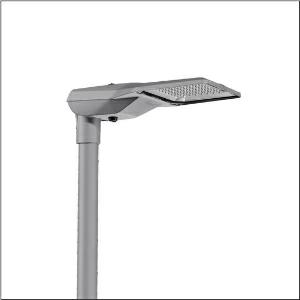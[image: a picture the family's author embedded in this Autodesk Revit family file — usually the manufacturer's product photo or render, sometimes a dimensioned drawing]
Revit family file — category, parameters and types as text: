
# Revit family: streetlight_sl_21_iq_midi___st1_0a_5xe3d31y08mb_3ca9
name_source: partatom
category: Lighting Fixtures
units: mm (PartAtom-declared; Revit-internal decimal feet)

## family parameters
Cut with Voids When Loaded = No
Host = Face
Light Source = No
Part Type = Normal
Room Calculation Point = No
Round Connector Dimension = Use Diameter
Shared = No

## types (1)
- --- (1 x LED, 18340 lm, 129.3 W, 3000K)
    Apparent Load = 129 VA
    CIE Flux Codes = 37 72 97 100 100
    Color Rendering = 70
    Color Temperature = 3000K
    Default Elevation = 1800 mm
    Description = Streetlight SL 21 iQ midi, mast luminaire, primary light control with lens, of PMMA, primary optical cover: cover, of toughened safety glass, transparent, light distribution: ST1.0a, light emission: direct distribution, primary light characteristic: asymmetric, installation type: post-top, side-entry, LED, High Power LED, rated luminous flux: 18.340lm, luminous efficacy: 142lm/W, light colour: 730, colour temperature: 3000K, control: presetting dimming logarithmic, Street-Remote, Auto-Match, Temp-Guard, Lumen-Switch, Night-Set, Smart-Wire, Light-Fading, Desk-Remote (wireless, voltage-free reading and setting of iQ features in the workshop via application-optimized NFC function/RFID function), optimised constant luminous flux control (CLO 2.0), mains connection: 230..240V, AC, 50/60Hz, start of lifetime: 129W, end of service life: 142W, reduction: 56W, luminaire housing, of diecast aluminium, powder-coated, Siteco® metallic grey (DB 702S), corrosivity category C5 mid according to DIN EN ISO 12944, please order mast flange separately, inclination adjustable: 0°, 5°, 10°, 15°, sealing non-destructively replaceable, multi-level sealing system, length: 644mm, width: 335mm, height: 110mm, mast flange for spigot size: 42mm (side-entry): 5XC10008XM4, 60/48mm (side-entry/post-top): 5XC10108XM2, 76/60mm (side-entry/post-top): 5XC10108XM1, Smart Interface below and above, protection rating (complete): IP66, insulation class (complete): insulation class II (safety insulation), certification: CE, ENEC, ENEC+, VDE, impact resistance: IK09, permissible operating ambient temperature for outdoor applications: -40..+50°C, standard-compliant lighting for roads and squares, packaging unit: 1 piece

Light Distribution: ST1.0a
    Height = 111 mm
    Lamp = 1 x LED
    Lamp Light Flux = 18340 lm
    Lamp Power = 129.3 W
    Lamp count = 1
    Length = 644 mm
    Luminous efficacy = 142 lm/W
    Manufacturer = Siteco
    ModVariant = No
    Model = 5XE3D31Y08MB
    Number of Poles = 1
    OnlyDefault = Yes
    Power Factor = 1
    Product Name = Streetlight SL 21 iQ midi | ST1.0a
    Product group = mast luminaire | pylon top
    ProductGroupID = 6100
    Protection Class = Protection class II
    Protection Degree = IP 66
    RLX_Detail_Level = 1
    RLX_Emergency_Light_Flux = 0 lm
    RLX_Emergency_Type = 0
    RLX_Emergency_Type_DB = No
    RlxData = <blob elided: 91429 chars, md5=f18d3c54>
    Socket = socket
    Standby Power = 0 W
    System Light Flux = 18340 lm
    System Power = 129 W
    Type Comments = factory setting: luminous flux: 100 % | dim-lin: 254 | 672 mA
    Type Image = l_1004304.jpg
    URL = http://relux.com
    VarID = @adj_062727
    Voltage = 0 V
    Weight = 0.00 kg
    Width = 336 mm

## geometry (parser evidence)
native form markers: Blend x4, Sweep x12
no freeform markers — native parametric forms only
